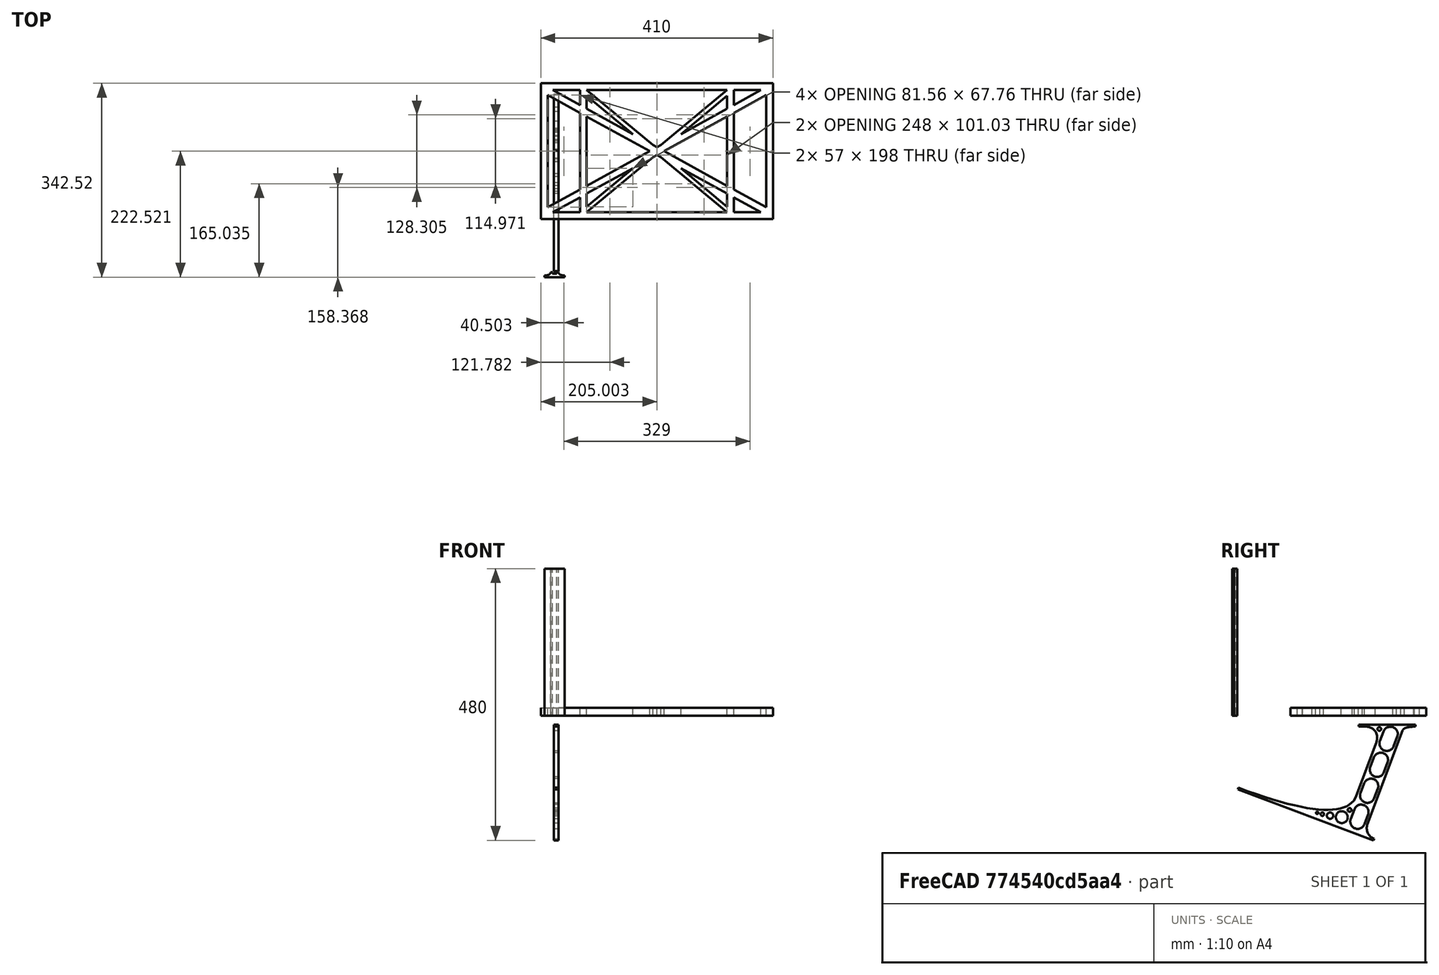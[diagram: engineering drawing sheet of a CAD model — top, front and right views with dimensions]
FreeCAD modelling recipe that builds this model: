
FCSTD DOCUMENT  (FreeCAD 0.19R0.19.2)
Label: laptopStand051
License: All rights reserved
LicenseURL: http://en.wikipedia.org/wiki/All_rights_reserved
objects: Sketcher::SketchObject×3, Part::Extrusion×3
note: 6 computed .brp shape members not serialized (recipe doc carries the construction recipe); baked Part::Feature solids carry a one-line shape summary decoded from their .brp

FEATURE [Sketcher::SketchObject] Sketch
  FullyConstrained = false
  sketch-geometry (94):
    g0: LineSegment StartX=-22.9272 StartY=136.221 StartZ=0 EndX=387.073 EndY=136.221 EndZ=0
    g1: LineSegment StartX=-22.9272 StartY=-103.779 StartZ=0 EndX=387.073 EndY=-103.779 EndZ=0
    g2: LineSegment StartX=375.073 StartY=115.221 StartZ=0 EndX=318.073 EndY=83.9235 EndZ=0
    g3: LineSegment StartX=-10.9272 StartY=-82.7794 StartZ=0 EndX=46.0728 EndY=-51.4823 EndZ=0
    g4: LineSegment StartX=-1.92719 StartY=124.221 StartZ=0 EndX=46.0728 EndY=97.8651 EndZ=0
    g5: LineSegment StartX=366.073 StartY=-91.7794 StartZ=0 EndX=318.073 EndY=-65.424 EndZ=0
    g6: LineSegment StartX=-10.9272 StartY=115.221 StartZ=0 EndX=-10.9272 EndY=-82.7794 EndZ=0
    g7: LineSegment StartX=375.073 StartY=-82.7794 StartZ=0 EndX=375.073 EndY=115.221 EndZ=0
    g8: LineSegment StartX=-1.92719 StartY=-91.7794 StartZ=0 EndX=46.0728 EndY=-91.7794 EndZ=0
    g9: LineSegment StartX=318.073 StartY=124.221 StartZ=0 EndX=366.073 EndY=124.221 EndZ=0
    g10: LineSegment StartX=306.073 StartY=-81.8102 StartZ=0 EndX=224.513 EndY=-14.0532 EndZ=0
    g11: LineSegment StartX=58.0728 StartY=114.251 StartZ=0 EndX=139.632 EndY=46.4944 EndZ=0
    g12: LineSegment StartX=306.073 StartY=124.221 StartZ=0 EndX=189.124 EndY=27.0628 EndZ=0
    g13: LineSegment StartX=58.0728 StartY=-91.7794 StartZ=0 EndX=175.022 EndY=5.37834 EndZ=0
    g14: LineSegment StartX=46.0728 StartY=124.221 StartZ=0 EndX=46.0728 EndY=97.8651 EndZ=0
    g15: LineSegment StartX=58.0728 StartY=-81.8102 StartZ=0 EndX=58.0728 EndY=-58.8351 EndZ=0
    g16: LineSegment StartX=318.073 StartY=124.221 StartZ=0 EndX=318.073 EndY=97.8651 EndZ=0
    g17: LineSegment StartX=306.073 StartY=114.251 StartZ=0 EndX=306.073 EndY=91.2763 EndZ=0
    g18: LineSegment StartX=224.513 StartY=46.4944 StartZ=0 EndX=306.073 EndY=114.251 EndZ=0
    g19: LineSegment StartX=175.022 StartY=27.0628 StartZ=0 EndX=58.0728 EndY=124.221 EndZ=0
    g20: LineSegment StartX=169.377 StartY=16.2206 StartZ=0 EndX=58.0728 EndY=77.3346 EndZ=0
    g21: LineSegment StartX=139.632 StartY=-14.0532 StartZ=0 EndX=58.0728 EndY=-81.8102 EndZ=0
    g22: LineSegment StartX=194.768 StartY=16.2206 StartZ=0 EndX=306.073 EndY=-44.8935 EndZ=0
    g23: LineSegment StartX=224.513 StartY=46.4944 StartZ=0 EndX=306.073 EndY=91.2763 EndZ=0
    g24: LineSegment StartX=139.632 StartY=-14.0532 StartZ=0 EndX=58.0728 EndY=-58.8351 EndZ=0
    g25: LineSegment StartX=189.124 StartY=5.37834 StartZ=0 EndX=185.124 EndY=7.57463 EndZ=0
    g26: LineSegment StartX=189.124 StartY=5.37834 StartZ=0 EndX=306.073 EndY=-91.7794 EndZ=0
    g27: LineSegment StartX=306.073 StartY=77.3346 StartZ=0 EndX=306.073 EndY=-44.8935 EndZ=0
    g28: LineSegment StartX=318.073 StartY=83.9235 StartZ=0 EndX=318.073 EndY=-51.4823 EndZ=0
    g29: LineSegment StartX=318.073 StartY=97.8651 StartZ=0 EndX=366.073 EndY=124.221 EndZ=0
    g30: LineSegment StartX=306.073 StartY=77.3346 StartZ=0 EndX=194.768 EndY=16.2206 EndZ=0
    g31: LineSegment StartX=306.073 StartY=-58.8351 StartZ=0 EndX=224.513 EndY=-14.0532 EndZ=0
    g32: LineSegment StartX=306.073 StartY=-58.8351 StartZ=0 EndX=306.073 EndY=-81.8102 EndZ=0
    g33: LineSegment StartX=318.073 StartY=-51.4823 StartZ=0 EndX=375.073 EndY=-82.7794 EndZ=0
    g34: LineSegment StartX=318.073 StartY=-65.424 StartZ=0 EndX=318.073 EndY=-91.7794 EndZ=0
    g35: LineSegment StartX=318.073 StartY=-91.7794 StartZ=0 EndX=366.073 EndY=-91.7794 EndZ=0
    g36: LineSegment StartX=58.0728 StartY=-44.8935 StartZ=0 EndX=58.0728 EndY=77.3346 EndZ=0
    g37: LineSegment StartX=46.0728 StartY=-65.424 StartZ=0 EndX=-1.92719 EndY=-91.7794 EndZ=0
    g38: LineSegment StartX=46.0728 StartY=-65.424 StartZ=0 EndX=46.0728 EndY=-91.7794 EndZ=0
    g39: LineSegment StartX=58.0728 StartY=-44.8935 StartZ=0 EndX=169.377 EndY=16.2206 EndZ=0
    g40: LineSegment StartX=58.0728 StartY=91.2763 StartZ=0 EndX=58.0728 EndY=114.251 EndZ=0
    g41: LineSegment StartX=46.0728 StartY=83.9235 StartZ=0 EndX=46.0728 EndY=-51.4823 EndZ=0
    g42: LineSegment StartX=46.0728 StartY=124.221 StartZ=0 EndX=-1.92719 EndY=124.221 EndZ=0
    g43: LineSegment StartX=58.0728 StartY=91.2763 StartZ=0 EndX=139.632 EndY=46.4944 EndZ=0
    g44: LineSegment StartX=46.0728 StartY=83.9235 StartZ=0 EndX=-10.9272 EndY=115.221 EndZ=0
    g45: LineSegment StartX=-22.9272 StartY=136.221 StartZ=0 EndX=-42.9272 EndY=136.221 EndZ=0
    g46: LineSegment StartX=387.073 StartY=136.221 StartZ=0 EndX=407.073 EndY=136.221 EndZ=0
    g47: LineSegment StartX=-42.9272 StartY=136.221 StartZ=0 EndX=-42.9272 EndY=-103.779 EndZ=0
    g48: LineSegment StartX=-22.9272 StartY=-103.779 StartZ=0 EndX=-42.9272 EndY=-103.779 EndZ=0
    g49: LineSegment StartX=407.073 StartY=136.221 StartZ=0 EndX=407.073 EndY=-103.779 EndZ=0
    g50: LineSegment StartX=387.073 StartY=-103.779 StartZ=0 EndX=407.073 EndY=-103.779 EndZ=0
    g51: LineSegment StartX=179.022 StartY=27.0628 StartZ=0 EndX=179.022 EndY=124.221 EndZ=0
    g52: LineSegment StartX=185.124 StartY=27.0628 StartZ=0 EndX=185.124 EndY=124.221 EndZ=0
    g53: LineSegment StartX=185.124 StartY=7.57463 StartZ=0 EndX=185.124 EndY=-91.7794 EndZ=0
    g54: LineSegment StartX=179.022 StartY=7.57463 StartZ=0 EndX=179.022 EndY=-91.7794 EndZ=0
    g55: LineSegment StartX=175.022 StartY=5.37834 StartZ=0 EndX=179.022 EndY=7.57463 EndZ=0
    g56: ArcOfCircle CenterX=-26.9272 CenterY=22.1087 CenterZ=0 NormalX=0 NormalY=0 NormalZ=1 AngleXU=0 Radius=8 StartAngle=1e-16 EndAngle=3.14159
    g57: ArcOfCircle CenterX=-26.9272 CenterY=-83.7794 CenterZ=0 NormalX=0 NormalY=0 NormalZ=1 AngleXU=0 Radius=8 StartAngle=3.14159 EndAngle=6.28319
    g58: LineSegment StartX=-34.9272 StartY=22.1087 StartZ=0 EndX=-34.9272 EndY=-83.7794 EndZ=0
    g59: LineSegment StartX=-18.9272 StartY=22.1087 StartZ=0 EndX=-18.9272 EndY=-83.7794 EndZ=0
    g60: LineSegment StartX=185.124 StartY=-91.7794 StartZ=0 EndX=306.073 EndY=-91.7794 EndZ=0
    g61: LineSegment StartX=179.022 StartY=-91.7794 StartZ=0 EndX=58.0728 EndY=-91.7794 EndZ=0
    g62: LineSegment StartX=306.073 StartY=124.221 StartZ=0 EndX=185.124 EndY=124.221 EndZ=0
    g63: LineSegment StartX=179.022 StartY=124.221 StartZ=0 EndX=58.0728 EndY=124.221 EndZ=0
    g64: ArcOfCircle CenterX=391.073 CenterY=22.1087 CenterZ=0 NormalX=0 NormalY=0 NormalZ=1 AngleXU=0 Radius=8 StartAngle=-4.4e-15 EndAngle=3.14159
    g65: LineSegment StartX=399.073 StartY=22.1087 StartZ=0 EndX=399.073 EndY=-83.7794 EndZ=0
    g66: LineSegment StartX=383.073 StartY=22.1087 StartZ=0 EndX=383.073 EndY=-83.7794 EndZ=0
    g67: ArcOfCircle CenterX=391.073 CenterY=-83.7794 CenterZ=0 NormalX=0 NormalY=0 NormalZ=1 AngleXU=0 Radius=8 StartAngle=3.14159 EndAngle=6.28319
    g68: Circle CenterX=175.022 CenterY=27.0628 CenterZ=0 NormalX=0 NormalY=0 NormalZ=1 AngleXU=0 Radius=1
    g69: Circle CenterX=179.022 CenterY=24.8665 CenterZ=0 NormalX=0 NormalY=0 NormalZ=1 AngleXU=0 Radius=1
    g70: Circle CenterX=179.022 CenterY=27.0628 CenterZ=0 NormalX=0 NormalY=0 NormalZ=1 AngleXU=0 Radius=1
    g71: BSplineCurve PolesCount=3 KnotsCount=2 Degree=2 IsPeriodic=0
    g72: GeomPoint X=175.022 Y=27.0628 Z=0
    g73: GeomPoint X=179.022 Y=27.0628 Z=0
    g74: Circle CenterX=189.124 CenterY=27.0628 CenterZ=0 NormalX=0 NormalY=0 NormalZ=1 AngleXU=0 Radius=1
    g75: Circle CenterX=185.124 CenterY=24.8665 CenterZ=0 NormalX=0 NormalY=0 NormalZ=1 AngleXU=0 Radius=1
    g76: Circle CenterX=185.124 CenterY=27.0628 CenterZ=0 NormalX=0 NormalY=0 NormalZ=1 AngleXU=0 Radius=1
    g77: BSplineCurve PolesCount=3 KnotsCount=2 Degree=2 IsPeriodic=0
    g78: GeomPoint X=189.124 Y=27.0628 Z=0
    g79: GeomPoint X=185.124 Y=27.0628 Z=0
    g80: LineSegment StartX=179.022 StartY=7.57463 StartZ=0 EndX=179.022 EndY=5.34704 EndZ=0
    g81: LineSegment StartX=185.124 StartY=7.57463 StartZ=0 EndX=185.124 EndY=5.34704 EndZ=0
    g82: Circle CenterX=175.022 CenterY=5.37834 CenterZ=0 NormalX=0 NormalY=0 NormalZ=1 AngleXU=0 Radius=1
    g83: Circle CenterX=179.022 CenterY=7.57463 CenterZ=0 NormalX=0 NormalY=0 NormalZ=1 AngleXU=0 Radius=1
    g84: Circle CenterX=179.022 CenterY=5.34704 CenterZ=0 NormalX=0 NormalY=0 NormalZ=1 AngleXU=0 Radius=1
    g85: BSplineCurve PolesCount=3 KnotsCount=2 Degree=2 IsPeriodic=0
    g86: GeomPoint X=175.022 Y=5.37834 Z=0
    g87: GeomPoint X=179.022 Y=5.34704 Z=0
    g88: Circle CenterX=189.124 CenterY=5.37834 CenterZ=0 NormalX=0 NormalY=0 NormalZ=1 AngleXU=0 Radius=1
    g89: Circle CenterX=185.124 CenterY=7.57463 CenterZ=0 NormalX=0 NormalY=0 NormalZ=1 AngleXU=0 Radius=1
    g90: Circle CenterX=185.124 CenterY=5.34704 CenterZ=0 NormalX=0 NormalY=0 NormalZ=1 AngleXU=0 Radius=1
    g91: BSplineCurve PolesCount=3 KnotsCount=2 Degree=2 IsPeriodic=0
    g92: GeomPoint X=189.124 Y=5.37834 Z=0
    g93: GeomPoint X=185.124 Y=5.34704 Z=0
  constraints (187):
    c: Horizontal(g0)
    c: Distance(g0) = 410
    c: Horizontal(g1)
    c: Block(g0)
    c: Horizontal(g8)
    c: Horizontal(g9)
    c: Tangent(g5,g20)
    c: PointOnObject(g20,g3)
    c: PointOnObject(g22,g2)
    c: Coincident(g43,g11)
    c: Coincident(g18,g23)
    c: Coincident(g24,g21)
    c: Coincident(g31,g10)
    c: Coincident(g26,g25)
    c: Coincident(g18,g17)
    c: Tangent(g17,g27)
    c: Tangent(g16,g28)
    c: Coincident(g23,g17)
    c: Tangent(g23,g29)
    c: Coincident(g2,g28)
    c: Coincident(g30,g27)
    c: Tangent(g2,g30)
    c: Coincident(g32,g10)
    c: Tangent(g5,g31)
    c: Tangent(g27,g32)
    c: Coincident(g22,g27)
    c: Tangent(g22,g33)
    c: Coincident(g28,g33)
    c: Coincident(g34,g5)
    c: Tangent(g28,g34)
    c: Coincident(g21,g15)
    c: Tangent(g15,g36)
    c: Coincident(g24,g15)
    c: Tangent(g24,g37)
    c: Coincident(g38,g37)
    c: Tangent(g14,g38)
    c: Coincident(g3,g41)
    c: Coincident(g39,g36)
    c: Tangent(g3,g39)
    c: Tangent(g36,g40)
    c: Tangent(g14,g41)
    c: Coincident(g11,g40)
    c: Coincident(g4,g14)
    c: Coincident(g43,g40)
    c: Tangent(g4,g43)
    c: Coincident(g20,g36)
    c: Coincident(g44,g41)
    c: Tangent(g20,g44)
    c: Block(g19)
    c: Block(g12)
    c: Block(g16)
    c: Block(g29)
    c: Block(g2)
    c: Block(g33)
    c: Block(g7)
    c: Block(g31)
    c: Block(g32)
    c: Block(g5)
    c: Block(g34)
    c: Block(g18)
    c: Block(g26)
    c: Block(g13)
    c: Block(g24)
    c: Block(g21)
    c: Block(g38)
    c: Block(g37)
    c: Block(g3)
    c: Block(g6)
    c: Block(g44)
    c: Block(g4)
    c: Block(g14)
    c: Block(g11)
    c: Block(g40)
    c: Block(g30)
    c: Block(g27)
    c: Block(g20)
    c: Block(g39)
    c: Block(g42)
    c: Block(g9)
    c: Block(g35)
    c: Block(g8)
    c: Horizontal(g45)
    c: Distance(g45) = 20
    c: Coincident(g46,g0)
    c: Horizontal(g46)
    c: Distance(g46) = 20
    c: Coincident(g47,g45)
    c: Vertical(g47)
    c: Horizontal(g48)
    c: Coincident(g48,g47)
    c: Coincident(g49,g46)
    c: Vertical(g49)
    c: Coincident(g50,g1)
    c: Horizontal(g50)
    c: Coincident(g50,g49)
    c: Block(g49)
    c: Block(g48)
    c: Block(g47)
    c: Block(g1)
    c: Vertical(g51)
    c: Vertical(g52)
    c: Coincident(g25,g53)
    c: Block(g51)
    c: Block(g52)
    c: Block(g54)
    c: Block(g53)
    c: Coincident(g55,g13)
    c: Coincident(g55,g54)
    c: Tangent(g56,g59) = 1.5708
    c: Tangent(g56,g58) = -1.5708
    c: Tangent(g58,g57) = -1.5708
    c: Tangent(g59,g57) = 1.5708
    c: Vertical(g58)
    c: Equal(g56,g57)
    c: Block(g59)
    c: Block(g58)
    c: Coincident(g60,g53)
    c: Coincident(g60,g26)
    c: Horizontal(g60)
    c: Coincident(g61,g54)
    c: Coincident(g61,g13)
    c: Horizontal(g61)
    c: Coincident(g62,g12)
    c: Coincident(g62,g52)
    c: Horizontal(g62)
    c: Coincident(g63,g51)
    c: Coincident(g63,g19)
    c: Horizontal(g63)
    c: Distance(g50) = 20
    c: Distance(g1) = 410
    c: Tangent(g64,g65) = 1.5708
    c: Tangent(g65,g67) = 1.5708
    c: Equal(g64,g67)
    c: Coincident(g66,g64)
    c: Coincident(g66,g67)
    c: Vertical(g66)
    c: Block(g65)
    c: Block(g66)
    c: Block(g22)
    c: Coincident(g71,g19)
    c: Weight(g68) = 1
    c: Equal(g68,g69)
    c: Equal(g68,g70)
    c: Coincident(g71,g51)
    c: InternalAlignment(g68,g71)
    c: InternalAlignment(g69,g71)
    c: InternalAlignment(g70,g71)
    c: InternalAlignment(g72,g71)
    c: InternalAlignment(g73,g71)
    c: Coincident(g77,g12)
    c: Weight(g74) = 1
    c: Equal(g74,g75)
    c: Equal(g74,g76)
    c: Coincident(g77,g52)
    c: InternalAlignment(g74,g77)
    c: InternalAlignment(g75,g77)
    c: InternalAlignment(g76,g77)
    c: InternalAlignment(g78,g77)
    c: InternalAlignment(g79,g77)
    c: Block(g77)
    c: Block(g71)
    c: Coincident(g80,g54)
    c: PointOnObject(g80,g54)
    c: PointOnObject(g81,g53)
    c: Coincident(g81,g25)
    c: Vertical(g81)
    c: Coincident(g85,g13)
    c: Weight(g82) = 1
    c: Equal(g82,g83)
    c: Coincident(g83,g54)
    c: Equal(g82,g84)
    c: Coincident(g85,g80)
    c: InternalAlignment(g82,g85)
    c: InternalAlignment(g83,g85)
    c: InternalAlignment(g84,g85)
    c: InternalAlignment(g86,g85)
    c: InternalAlignment(g87,g85)
    c: Coincident(g91,g25)
    c: Weight(g88) = 1
    c: Equal(g88,g89)
    c: Coincident(g89,g25)
    c: Equal(g88,g90)
    c: InternalAlignment(g88,g91)
    c: InternalAlignment(g89,g91)
    c: InternalAlignment(g90,g91)
    c: InternalAlignment(g92,g91)
    c: InternalAlignment(g93,g91)
FEATURE [Sketcher::SketchObject] Sketch001
  FullyConstrained = true
  MapMode = 4
  Placement = pos=(0,0,0) rot=(0.57735,0.57735,0.57735;2.0944rad)
  Support = -> [Sketch]
  sketch-geometry (46):
    g0: BSplineCurve PolesCount=3 KnotsCount=2 Degree=2 IsPeriodic=0
    g1: ArcOfCircle CenterX=73.122 CenterY=-32.2909 CenterZ=0 NormalX=0 NormalY=0 NormalZ=1 AngleXU=0 Radius=13 StartAngle=5.92268 EndAngle=9.06428
    g2: ArcOfCircle CenterX=66.7816 CenterY=-49.1439 CenterZ=0 NormalX=0 NormalY=0 NormalZ=1 AngleXU=0 Radius=13 StartAngle=2.78068 EndAngle=5.92131
    g3: ArcOfCircle CenterX=55.9263 CenterY=-78.1807 CenterZ=0 NormalX=0 NormalY=0 NormalZ=1 AngleXU=0 Radius=13 StartAngle=5.92268 EndAngle=9.06428
    g4: ArcOfCircle CenterX=49.5884 CenterY=-95.0342 CenterZ=0 NormalX=0 NormalY=0 NormalZ=1 AngleXU=0 Radius=13 StartAngle=2.78068 EndAngle=5.92131
    g5: ArcOfCircle CenterX=38.7206 CenterY=-124.067 CenterZ=0 NormalX=0 NormalY=0 NormalZ=1 AngleXU=0 Radius=13 StartAngle=5.92268 EndAngle=9.06428
    g6: ArcOfCircle CenterX=32.3875 CenterY=-140.92 CenterZ=0 NormalX=0 NormalY=0 NormalZ=1 AngleXU=0 Radius=13 StartAngle=2.78068 EndAngle=5.92131
    g7: ArcOfCircle CenterX=21.4715 CenterY=-169.934 CenterZ=0 NormalX=0 NormalY=0 NormalZ=1 AngleXU=0 Radius=13 StartAngle=5.92268 EndAngle=9.06428
    g8: ArcOfCircle CenterX=15.1336 CenterY=-186.787 CenterZ=0 NormalX=0 NormalY=0 NormalZ=1 AngleXU=0 Radius=13 StartAngle=2.78068 EndAngle=5.92131
    g9-g12: Circle x4 (B-spline internal-alignment scaffolding for g13; pole/knot coordinates omitted)
    g13: BSplineCurve PolesCount=4 KnotsCount=2 Degree=3 IsPeriodic=0
    g14: GeomPoint X=28.8094 Y=-19.0875 Z=0
    g15: GeomPoint X=47.0443 Y=-50.4712 Z=0
    g16: Circle CenterX=53.5586 CenterY=-23.2695 CenterZ=0 NormalX=0 NormalY=0 NormalZ=1 AngleXU=0 Radius=3.24518
    g17: Circle CenterX=-195.441 CenterY=-127.082 CenterZ=0 NormalX=0 NormalY=0 NormalZ=1 AngleXU=0 Radius=1
    g18: Circle CenterX=-8.24091 CenterY=-197.481 CenterZ=0 NormalX=0 NormalY=0 NormalZ=1 AngleXU=0 Radius=1
    g19: Circle CenterX=12.8789 CenterY=-141.321 CenterZ=0 NormalX=0 NormalY=0 NormalZ=1 AngleXU=0 Radius=1
    g20: BSplineCurve PolesCount=3 KnotsCount=2 Degree=2 IsPeriodic=0
    g21: GeomPoint X=-195.441 Y=-127.082 Z=0
    g22: GeomPoint X=12.8789 Y=-141.321 Z=0
    g23: Circle CenterX=-12.8016 CenterY=-179.036 CenterZ=0 NormalX=0 NormalY=0 NormalZ=1 AngleXU=0 Radius=10.5072
    g24: Circle CenterX=0.933922 CenterY=-166.43 CenterZ=0 NormalX=0 NormalY=0 NormalZ=1 AngleXU=0 Radius=3.26661
    g25: Circle CenterX=-33.5518 CenterY=-176.44 CenterZ=0 NormalX=0 NormalY=0 NormalZ=1 AngleXU=0 Radius=5.64388
    g26: Circle CenterX=-47.2366 CenterY=-173.859 CenterZ=0 NormalX=0 NormalY=0 NormalZ=1 AngleXU=0 Radius=3.01653
    g27: Circle CenterX=-56.2595 CenterY=-171.456 CenterZ=0 NormalX=0 NormalY=0 NormalZ=1 AngleXU=0 Radius=2.12826
    g28: ArcOfCircle CenterX=51.2151 CenterY=-198.473 CenterZ=0 NormalX=0 NormalY=0 NormalZ=1 AngleXU=0 Radius=20 StartAngle=2.78189 EndAngle=4.35269
    g29: LineSegment StartX=32.4951 StartY=-191.433 StartZ=0 EndX=94.6577 EndY=-26.1351 EndZ=0
    g30: LineSegment StartX=43.1192 StartY=-220.001 StartZ=0 EndX=-196.497 EndY=-129.89 EndZ=0
    g31: LineSegment StartX=43.1192 StartY=-220.001 StartZ=0 EndX=44.1752 EndY=-217.193 EndZ=0
    g32: LineSegment StartX=117.223 StartY=-19.0875 StartZ=0 EndX=117.223 EndY=-16.0875 EndZ=0
    g33: LineSegment StartX=117.223 StartY=-16.0875 StartZ=0 EndX=17.2232 EndY=-16.0875 EndZ=0
    g34: LineSegment StartX=17.2232 StartY=-16.0875 StartZ=0 EndX=17.2232 EndY=-19.0875 EndZ=0
    g35: LineSegment StartX=28.8094 StartY=-19.0875 StartZ=0 EndX=17.2232 EndY=-19.0875 EndZ=0
    g36: LineSegment StartX=47.0443 StartY=-50.4712 StartZ=0 EndX=12.8789 EndY=-141.321 EndZ=0
    g37: LineSegment StartX=-195.441 StartY=-127.082 StartZ=0 EndX=-196.497 EndY=-129.89 EndZ=0
    g38: LineSegment StartX=85.2864 StartY=-36.8765 StartZ=0 EndX=78.9396 EndY=-53.7463 EndZ=0
    g39: LineSegment StartX=60.9577 StartY=-27.7052 StartZ=0 EndX=54.6191 EndY=-44.5532 EndZ=0
    g40: LineSegment StartX=68.0907 StartY=-82.7664 StartZ=0 EndX=61.7465 EndY=-99.6365 EndZ=0
    g41: LineSegment StartX=43.7619 StartY=-73.595 StartZ=0 EndX=37.426 EndY=-90.4435 EndZ=0
    g42: LineSegment StartX=50.885 StartY=-128.652 StartZ=0 EndX=44.5456 EndY=-145.522 EndZ=0
    g43: LineSegment StartX=26.5562 StartY=-119.481 StartZ=0 EndX=20.2251 EndY=-136.329 EndZ=0
    g44: LineSegment StartX=9.3071 StartY=-165.349 StartZ=0 EndX=2.97115 EndY=-182.197 EndZ=0
    g45: LineSegment StartX=33.6358 StartY=-174.52 StartZ=0 EndX=27.2917 EndY=-191.39 EndZ=0
  constraints (70):
    c: Block(g0)
    c: Block(g1)
    c: Block(g2)
    c: Block(g4)
    c: Block(g3)
    c: Block(g6)
    c: Block(g5)
    c: Block(g8)
    c: Block(g7)
    c: Weight(g9) = 1
    c: Equal(g9,g10)
    c: Equal(g9,g11)
    c: Equal(g9,g12)
    c: InternalAlignment(g9-g12 -> g13) x4
    c: InternalAlignment(g14,g13)
    c: InternalAlignment(g15,g13)
    c: Block(g16)
    c: Weight(g17) = 1
    c: Equal(g17,g18)
    c: Equal(g17,g19)
    c: InternalAlignment(g17,g20)
    c: InternalAlignment(g18,g20)
    c: InternalAlignment(g19,g20)
    c: InternalAlignment(g21,g20)
    c: InternalAlignment(g22,g20)
    c: Block(g20)
    c: Block(g23)
    c: Block(g24)
    c: Block(g25)
    c: Block(g26)
    c: Block(g27)
    c: Block(g28)
    c: Coincident(g29,g28)
    c: Coincident(g29,g0)
    c: Block(g13)
    c: Coincident(g31,g30)
    c: Coincident(g31,g28)
    c: Block(g31)
    c: Coincident(g32,g0)
    c: Vertical(g32)
    c: Coincident(g33,g32)
    c: Horizontal(g33)
    c: Coincident(g34,g33)
    c: Vertical(g34)
    c: Block(g33)
    c: Coincident(g35,g13)
    c: Coincident(g35,g34)
    c: Horizontal(g35)
    c: Coincident(g36,g13)
    c: Coincident(g36,g20)
    c: Coincident(g37,g20)
    c: Coincident(g37,g30)
    c: Block(g30)
    c: Coincident(g38,g1)
    c: Coincident(g38,g2)
    c: Coincident(g39,g1)
    c: Coincident(g39,g2)
    c: Coincident(g40,g3)
    c: Coincident(g40,g4)
    c: Coincident(g41,g3)
    c: Coincident(g41,g4)
    c: Coincident(g42,g5)
    c: Coincident(g42,g6)
    c: Coincident(g43,g5)
    c: Coincident(g43,g6)
    c: Coincident(g44,g7)
    c: Coincident(g44,g8)
    c: Coincident(g45,g7)
    c: Coincident(g45,g8)
    c: Distance(g30) = 256
FEATURE [Part::Extrusion] Extrude002
  Base = -> Sketch001
  Dir = (1,0,0)
  DirMode = 2
  FaceMakerClass = Part::FaceMakerBullseye
  LengthFwd = 8
  LengthRev = 0
  Solid = true
  Symmetric = false
FEATURE [Sketcher::SketchObject] Sketch002
  FullyConstrained = true
  sketch-geometry (20):
    g0: LineSegment StartX=-2.77179 StartY=-200.304 StartZ=0 EndX=5.22821 EndY=-200.304 EndZ=0
    g1: LineSegment StartX=5.22821 StartY=-200.304 StartZ=0 EndX=5.22821 EndY=-197.304 EndZ=0
    g2: LineSegment StartX=-2.77179 StartY=-200.304 StartZ=0 EndX=-2.77179 EndY=-197.304 EndZ=0
    g3: LineSegment StartX=5.22821 StartY=-197.304 StartZ=0 EndX=8.22821 EndY=-197.304 EndZ=0
    g4: LineSegment StartX=-2.77179 StartY=-197.304 StartZ=0 EndX=-5.77179 EndY=-197.304 EndZ=0
    g5: LineSegment StartX=19.2282 StartY=-203.304 StartZ=0 EndX=19.2282 EndY=-206.304 EndZ=0
    g6: LineSegment StartX=-16.7718 StartY=-203.304 StartZ=0 EndX=-16.7718 EndY=-206.304 EndZ=0
    g7: LineSegment StartX=-16.7718 StartY=-206.304 StartZ=0 EndX=19.2282 EndY=-206.304 EndZ=0
    g8: Circle CenterX=-16.7718 CenterY=-203.304 CenterZ=0 NormalX=0 NormalY=0 NormalZ=1 AngleXU=0 Radius=1
    g9: Circle CenterX=-5.77179 CenterY=-203.304 CenterZ=0 NormalX=0 NormalY=0 NormalZ=1 AngleXU=0 Radius=1
    g10: Circle CenterX=-5.77179 CenterY=-197.304 CenterZ=0 NormalX=0 NormalY=0 NormalZ=1 AngleXU=0 Radius=1
    g11: BSplineCurve PolesCount=3 KnotsCount=2 Degree=2 IsPeriodic=0
    g12: GeomPoint X=-16.7718 Y=-203.304 Z=0
    g13: GeomPoint X=-5.77179 Y=-197.304 Z=0
    g14: Circle CenterX=19.2282 CenterY=-203.304 CenterZ=0 NormalX=0 NormalY=0 NormalZ=1 AngleXU=0 Radius=1
    g15: Circle CenterX=8.22821 CenterY=-203.304 CenterZ=0 NormalX=0 NormalY=0 NormalZ=1 AngleXU=0 Radius=1
    g16: Circle CenterX=8.22821 CenterY=-197.304 CenterZ=0 NormalX=0 NormalY=0 NormalZ=1 AngleXU=0 Radius=1
    g17: BSplineCurve PolesCount=3 KnotsCount=2 Degree=2 IsPeriodic=0
    g18: GeomPoint X=19.2282 Y=-203.304 Z=0
    g19: GeomPoint X=8.22821 Y=-197.304 Z=0
  constraints (41):
    c: Horizontal(g0)
    c: Distance(g0) = 8
    c: Coincident(g1,g0)
    c: Vertical(g1)
    c: Distance(g1) = 3
    c: Coincident(g2,g0)
    c: Vertical(g2)
    c: Distance(g2) = 3
    c: Coincident(g3,g1)
    c: Horizontal(g3)
    c: Distance(g3) = 3
    c: Coincident(g4,g2)
    c: Horizontal(g4)
    c: Distance(g4) = 3
    c: Vertical(g5)
    c: Vertical(g6)
    c: Coincident(g7,g6)
    c: Coincident(g7,g5)
    c: Weight(g8) = 1
    c: Equal(g8,g9)
    c: Equal(g8,g10)
    c: Coincident(g11,g4)
    c: InternalAlignment(g8,g11)
    c: InternalAlignment(g9,g11)
    c: InternalAlignment(g10,g11)
    c: InternalAlignment(g12,g11)
    c: InternalAlignment(g13,g11)
    c: Coincident(g17,g5)
    c: Weight(g14) = 1
    c: Equal(g14,g15)
    c: Equal(g14,g16)
    c: Coincident(g17,g3)
    c: InternalAlignment(g14,g17)
    c: InternalAlignment(g15,g17)
    c: InternalAlignment(g16,g17)
    c: InternalAlignment(g18,g17)
    c: InternalAlignment(g19,g17)
    c: Block(g7)
    c: Block(g17)
    c: Block(g11)
    c: Block(g6)
FEATURE [Part::Extrusion] Extrude003
  Base = -> Sketch002
  Dir = (0,0,1)
  DirMode = 2
  FaceMakerClass = Part::FaceMakerBullseye
  LengthFwd = 260
  LengthRev = 0
  Solid = true
  Symmetric = false
FEATURE [Part::Extrusion] Extrude
  Base = -> Sketch
  Dir = (0,0,1)
  DirMode = 2
  FaceMakerClass = Part::FaceMakerBullseye
  LengthFwd = 14
  LengthRev = 0
  Solid = true
  Symmetric = false
